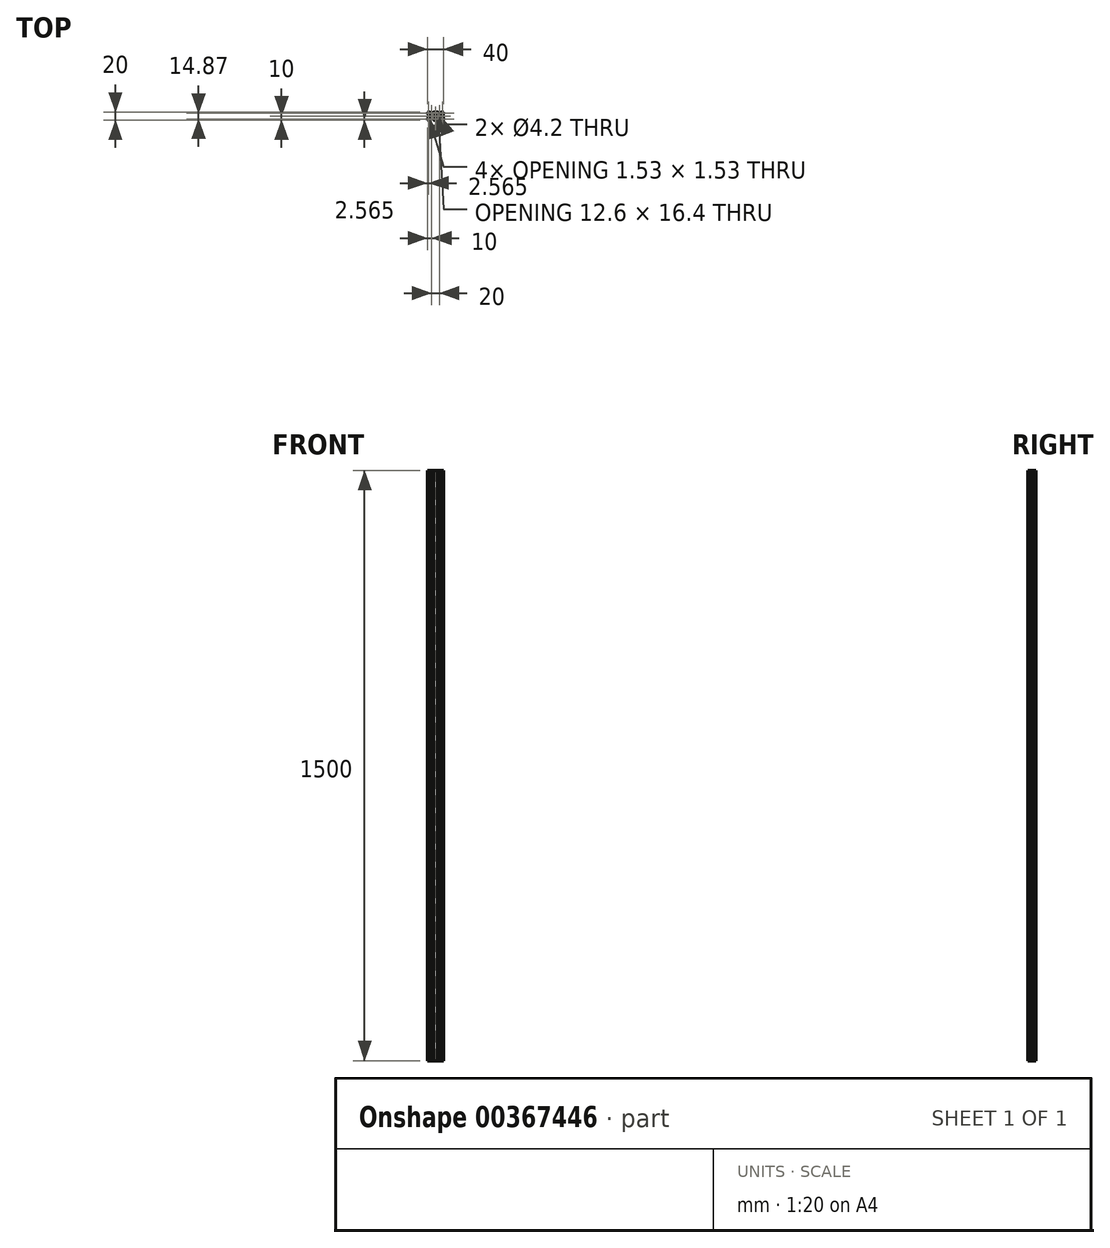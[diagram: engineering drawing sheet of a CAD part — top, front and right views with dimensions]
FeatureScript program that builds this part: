
annotation { "Feature Type Name" : "Feature", "Feature Type Description" : "" }
export const myFeature = defineFeature(function(context is Context, id is Id, definition is map)
    precondition{}
    {
        {
            var Q0;
            Q0=qCreatedBy(makeId("Top.planeOp"),FACE);
            var sketch = newSketch(context, id + "F0", { "sketchPlane" : qUnion([Q0])});
            skLineSegment(sketch, "E0.bottom", {"start": v(0, 0) * mm, "end": v(5.2, 0) * mm});
            skLineSegment(sketch, "E0.top", {"start": v(0, 20) * mm, "end": v(5.2, 20) * mm});
            skLineSegment(sketch, "E0.left", {"start": v(0, 0) * mm, "end": v(0, 5.2) * mm});
            skLineSegment(sketch, "E0.right", {"start": v(40, 0) * mm, "end": v(40, 5.2) * mm});
            skLineSegment(sketch, "E1", {"start": v(33.8, 12.84) * mm, "end": v(33.8, 7.16) * mm});
            skLineSegment(sketch, "E2", {"start": v(33.8, 12.84) * mm, "end": v(36.56, 15.6) * mm});
            skLineSegment(sketch, "E3", {"start": v(33.8, 7.16) * mm, "end": v(36.56, 4.4) * mm});
            skLineSegment(sketch, "E4", {"start": v(36.56, 15.6) * mm, "end": v(38.2, 15.6) * mm});
            skLineSegment(sketch, "E5", {"start": v(36.56, 4.4) * mm, "end": v(38.2, 4.4) * mm});
            skLineSegment(sketch, "E6", {"start": v(38.2, 13) * mm, "end": v(38.2, 15.6) * mm});
            skLineSegment(sketch, "E7", {"start": v(38.2, 7) * mm, "end": v(38.2, 4.4) * mm});
            skLineSegment(sketch, "E8.trimOffspring", {"start": v(40, 14.8) * mm, "end": v(40, 20) * mm});
            skLineSegment(sketch, "E9", {"start": v(33, 18.2) * mm, "end": v(35.6, 18.2) * mm});
            skLineSegment(sketch, "E10", {"start": v(35.6, 18.2) * mm, "end": v(35.6, 16.56) * mm});
            skLineSegment(sketch, "E11", {"start": v(35.6, 16.56) * mm, "end": v(32.84, 13.8) * mm});
            skLineSegment(sketch, "E12", {"start": v(32.84, 13.8) * mm, "end": v(27.16, 13.8) * mm});
            skLineSegment(sketch, "E13", {"start": v(27, 18.2) * mm, "end": v(24.4, 18.2) * mm});
            skLineSegment(sketch, "E14", {"start": v(24.4, 18.2) * mm, "end": v(24.4, 16.56) * mm});
            skLineSegment(sketch, "E15", {"start": v(24.4, 16.56) * mm, "end": v(27.16, 13.8) * mm});
            skLineSegment(sketch, "E16", {"start": v(33, 1.8) * mm, "end": v(35.6, 1.8) * mm});
            skLineSegment(sketch, "E17", {"start": v(35.6, 1.8) * mm, "end": v(35.6, 3.44) * mm});
            skLineSegment(sketch, "E18", {"start": v(35.6, 3.44) * mm, "end": v(32.84, 6.2) * mm});
            skLineSegment(sketch, "E19", {"start": v(32.84, 6.2) * mm, "end": v(27.16, 6.2) * mm});
            skLineSegment(sketch, "E20", {"start": v(27.16, 6.2) * mm, "end": v(24.4, 3.44) * mm});
            skLineSegment(sketch, "E21", {"start": v(24.4, 3.44) * mm, "end": v(24.4, 1.8) * mm});
            skLineSegment(sketch, "E22", {"start": v(24.4, 1.8) * mm, "end": v(27, 1.8) * mm});
            skLineSegment(sketch, "E23.trimOffspring", {"start": v(34.8, 20) * mm, "end": v(40, 20) * mm});
            skLineSegment(sketch, "E24.trimOffspring", {"start": v(34.8, 0) * mm, "end": v(40, 0) * mm});
            skLineSegment(sketch, "E25", {"start": v(7, 18.2) * mm, "end": v(4.4, 18.2) * mm});
            skLineSegment(sketch, "E26", {"start": v(4.4, 18.2) * mm, "end": v(4.4, 16.56) * mm});
            skLineSegment(sketch, "E27", {"start": v(4.4, 16.56) * mm, "end": v(7.16, 13.8) * mm});
            skLineSegment(sketch, "E28", {"start": v(7.16, 13.8) * mm, "end": v(12.84, 13.8) * mm});
            skLineSegment(sketch, "E29", {"start": v(12.84, 13.8) * mm, "end": v(15.6, 16.56) * mm});
            skLineSegment(sketch, "E30", {"start": v(15.6, 16.56) * mm, "end": v(15.6, 18.2) * mm});
            skLineSegment(sketch, "E31", {"start": v(15.6, 18.2) * mm, "end": v(13, 18.2) * mm});
            skLineSegment(sketch, "E32", {"start": v(1.8, 13) * mm, "end": v(1.8, 15.6) * mm});
            skLineSegment(sketch, "E33", {"start": v(1.8, 15.6) * mm, "end": v(3.44, 15.6) * mm});
            skLineSegment(sketch, "E34", {"start": v(3.44, 15.6) * mm, "end": v(6.2, 12.84) * mm});
            skLineSegment(sketch, "E35", {"start": v(6.2, 12.84) * mm, "end": v(6.2, 7.16) * mm});
            skLineSegment(sketch, "E36", {"start": v(6.2, 7.16) * mm, "end": v(3.44, 4.4) * mm});
            skLineSegment(sketch, "E37", {"start": v(3.44, 4.4) * mm, "end": v(1.8, 4.4) * mm});
            skLineSegment(sketch, "E38", {"start": v(1.8, 7) * mm, "end": v(1.8, 4.4) * mm});
            skLineSegment(sketch, "E39", {"start": v(7, 1.8) * mm, "end": v(4.4, 1.8) * mm});
            skLineSegment(sketch, "E40", {"start": v(4.4, 1.8) * mm, "end": v(4.4, 3.44) * mm});
            skLineSegment(sketch, "E41", {"start": v(4.4, 3.44) * mm, "end": v(7.16, 6.2) * mm});
            skLineSegment(sketch, "E42", {"start": v(7.16, 6.2) * mm, "end": v(12.84, 6.2) * mm});
            skLineSegment(sketch, "E43", {"start": v(12.84, 6.2) * mm, "end": v(15.6, 3.44) * mm});
            skLineSegment(sketch, "E44", {"start": v(15.6, 3.44) * mm, "end": v(15.6, 1.8) * mm});
            skLineSegment(sketch, "E45", {"start": v(15.6, 1.8) * mm, "end": v(13, 1.8) * mm});
            skLineSegment(sketch, "E46.trimOffspring", {"start": v(14.8, 20) * mm, "end": v(25.2, 20) * mm});
            skLineSegment(sketch, "E47.trimOffspring", {"start": v(0, 14.8) * mm, "end": v(0, 20) * mm});
            skLineSegment(sketch, "E48.trimOffspring", {"start": v(14.8, 0) * mm, "end": v(25.2, 0) * mm});
            skLineSegment(sketch, "E49", {"start": v(38.2, 7) * mm, "end": v(40, 5.2) * mm});
            skLineSegment(sketch, "E50", {"start": v(38.2, 13) * mm, "end": v(40, 14.8) * mm});
            skLineSegment(sketch, "E51", {"start": v(33, 1.8) * mm, "end": v(34.8, 0) * mm});
            skLineSegment(sketch, "E52", {"start": v(27, 1.8) * mm, "end": v(25.2, 0) * mm});
            skLineSegment(sketch, "E53", {"start": v(13, 1.8) * mm, "end": v(14.8, 0) * mm});
            skLineSegment(sketch, "E54", {"start": v(7, 1.8) * mm, "end": v(5.2, 0) * mm});
            skLineSegment(sketch, "E55", {"start": v(1.8, 7) * mm, "end": v(0, 5.2) * mm});
            skLineSegment(sketch, "E56", {"start": v(1.8, 13) * mm, "end": v(0, 14.8) * mm});
            skLineSegment(sketch, "E57", {"start": v(7, 18.2) * mm, "end": v(5.2, 20) * mm});
            skLineSegment(sketch, "E58", {"start": v(13, 18.2) * mm, "end": v(14.8, 20) * mm});
            skLineSegment(sketch, "E59", {"start": v(27, 18.2) * mm, "end": v(25.2, 20) * mm});
            skLineSegment(sketch, "E60", {"start": v(33, 18.2) * mm, "end": v(34.8, 20) * mm});
            skPoint(sketch, "E61.start.orphan", {"position": v(7, 0) * mm});
            skSolve(sketch);
        }
        {
            var Q0;
            Q0=qSketchRegion(id+"F0",true);
            extrude(context, id + "F1", {"entities" : qUnion([Q0]), "depth" : 1500 * mm});
        }
        {
            var Q0;
            Q0=makeQuery(id+"F1.opExtrude","CAP_FACE",FACE,{"disambiguationData":[OSD([sQuery(id+"F0.wireOp",EDGE,"E0.bottom"),sQuery(id+"F0.wireOp",EDGE,"E0.top"),sQuery(id+"F0.wireOp",EDGE,"E0.left"),sQuery(id+"F0.wireOp",EDGE,"E0.right"),sQuery(id+"F0.wireOp",EDGE,"E1"),sQuery(id+"F0.wireOp",EDGE,"E2"),sQuery(id+"F0.wireOp",EDGE,"E3"),sQuery(id+"F0.wireOp",EDGE,"E4"),sQuery(id+"F0.wireOp",EDGE,"E5"),sQuery(id+"F0.wireOp",EDGE,"E6"),sQuery(id+"F0.wireOp",EDGE,"E7"),sQuery(id+"F0.wireOp",EDGE,"E8.trimOffspring"),sQuery(id+"F0.wireOp",EDGE,"E9"),sQuery(id+"F0.wireOp",EDGE,"E10"),sQuery(id+"F0.wireOp",EDGE,"E11"),sQuery(id+"F0.wireOp",EDGE,"E12"),sQuery(id+"F0.wireOp",EDGE,"E13"),sQuery(id+"F0.wireOp",EDGE,"E14"),sQuery(id+"F0.wireOp",EDGE,"E15"),sQuery(id+"F0.wireOp",EDGE,"E16"),sQuery(id+"F0.wireOp",EDGE,"E17"),sQuery(id+"F0.wireOp",EDGE,"E18"),sQuery(id+"F0.wireOp",EDGE,"E19"),sQuery(id+"F0.wireOp",EDGE,"E20"),sQuery(id+"F0.wireOp",EDGE,"E21"),sQuery(id+"F0.wireOp",EDGE,"E22"),sQuery(id+"F0.wireOp",EDGE,"E23.trimOffspring"),sQuery(id+"F0.wireOp",EDGE,"E24.trimOffspring"),sQuery(id+"F0.wireOp",EDGE,"E25"),sQuery(id+"F0.wireOp",EDGE,"E26"),sQuery(id+"F0.wireOp",EDGE,"E27"),sQuery(id+"F0.wireOp",EDGE,"E28"),sQuery(id+"F0.wireOp",EDGE,"E29"),sQuery(id+"F0.wireOp",EDGE,"E30"),sQuery(id+"F0.wireOp",EDGE,"E31"),sQuery(id+"F0.wireOp",EDGE,"E32"),sQuery(id+"F0.wireOp",EDGE,"E33"),sQuery(id+"F0.wireOp",EDGE,"E34"),sQuery(id+"F0.wireOp",EDGE,"E35"),sQuery(id+"F0.wireOp",EDGE,"E36"),sQuery(id+"F0.wireOp",EDGE,"E37"),sQuery(id+"F0.wireOp",EDGE,"E38"),sQuery(id+"F0.wireOp",EDGE,"E39"),sQuery(id+"F0.wireOp",EDGE,"E40"),sQuery(id+"F0.wireOp",EDGE,"E41"),sQuery(id+"F0.wireOp",EDGE,"E42"),sQuery(id+"F0.wireOp",EDGE,"E43"),sQuery(id+"F0.wireOp",EDGE,"E44"),sQuery(id+"F0.wireOp",EDGE,"E45"),sQuery(id+"F0.wireOp",EDGE,"E46.trimOffspring"),sQuery(id+"F0.wireOp",EDGE,"E47.trimOffspring"),sQuery(id+"F0.wireOp",EDGE,"E48.trimOffspring"),sQuery(id+"F0.wireOp",EDGE,"E49"),sQuery(id+"F0.wireOp",EDGE,"E50"),sQuery(id+"F0.wireOp",EDGE,"E51"),sQuery(id+"F0.wireOp",EDGE,"E52"),sQuery(id+"F0.wireOp",EDGE,"E53"),sQuery(id+"F0.wireOp",EDGE,"E54"),sQuery(id+"F0.wireOp",EDGE,"E55"),sQuery(id+"F0.wireOp",EDGE,"E56"),sQuery(id+"F0.wireOp",EDGE,"E57"),sQuery(id+"F0.wireOp",EDGE,"E58"),sQuery(id+"F0.wireOp",EDGE,"E59"),sQuery(id+"F0.wireOp",EDGE,"E60")])],"isStart":false});
            var sketch = newSketch(context, id + "F2", { "sketchPlane" : qUnion([Q0])});
            skLineSegment(sketch, "E62", {"start": v(1.8, 18.2) * mm, "end": v(1.8, 16.67) * mm});
            skLineSegment(sketch, "E63", {"start": v(1.8, 16.67) * mm, "end": v(3.33, 18.2) * mm});
            skLineSegment(sketch, "E64", {"start": v(3.33, 18.2) * mm, "end": v(1.8, 18.2) * mm});
            skLineSegment(sketch, "E65", {"start": v(1.8, 1.8) * mm, "end": v(3.33, 1.8) * mm});
            skLineSegment(sketch, "E66", {"start": v(3.33, 1.8) * mm, "end": v(1.8, 3.33) * mm});
            skLineSegment(sketch, "E67", {"start": v(1.8, 3.33) * mm, "end": v(1.8, 1.8) * mm});
            skLineSegment(sketch, "E68", {"start": v(38.2, 1.8) * mm, "end": v(38.2, 3.33) * mm});
            skLineSegment(sketch, "E69", {"start": v(38.2, 3.33) * mm, "end": v(36.67, 1.8) * mm});
            skLineSegment(sketch, "E70", {"start": v(36.67, 1.8) * mm, "end": v(38.2, 1.8) * mm});
            skLineSegment(sketch, "E71", {"start": v(38.2, 18.2) * mm, "end": v(38.2, 16.67) * mm});
            skLineSegment(sketch, "E72", {"start": v(38.2, 16.67) * mm, "end": v(36.67, 18.2) * mm});
            skLineSegment(sketch, "E73", {"start": v(36.67, 18.2) * mm, "end": v(38.2, 18.2) * mm});
            skSolve(sketch);
        }
        {
            var Q0;
            Q0=qSketchRegion(id+"F2",true);
            extrude(context, id + "F3", {"entities" : qUnion([Q0]), "operationType" : NewBodyOperationType.REMOVE, "endBound" : BoundingType.THROUGH_ALL, "oppositeDirection" : true, "depth" : 25 * mm});
        }
        {
            var Q0;
            Q0=makeQuery(id+"F1.opExtrude","CAP_FACE",FACE,{"disambiguationData":[OSD([sQuery(id+"F0.wireOp",EDGE,"E0.bottom"),sQuery(id+"F0.wireOp",EDGE,"E0.top"),sQuery(id+"F0.wireOp",EDGE,"E0.left"),sQuery(id+"F0.wireOp",EDGE,"E0.right"),sQuery(id+"F0.wireOp",EDGE,"E1"),sQuery(id+"F0.wireOp",EDGE,"E2"),sQuery(id+"F0.wireOp",EDGE,"E3"),sQuery(id+"F0.wireOp",EDGE,"E4"),sQuery(id+"F0.wireOp",EDGE,"E5"),sQuery(id+"F0.wireOp",EDGE,"E6"),sQuery(id+"F0.wireOp",EDGE,"E7"),sQuery(id+"F0.wireOp",EDGE,"E8.trimOffspring"),sQuery(id+"F0.wireOp",EDGE,"E9"),sQuery(id+"F0.wireOp",EDGE,"E10"),sQuery(id+"F0.wireOp",EDGE,"E11"),sQuery(id+"F0.wireOp",EDGE,"E12"),sQuery(id+"F0.wireOp",EDGE,"E13"),sQuery(id+"F0.wireOp",EDGE,"E14"),sQuery(id+"F0.wireOp",EDGE,"E15"),sQuery(id+"F0.wireOp",EDGE,"E16"),sQuery(id+"F0.wireOp",EDGE,"E17"),sQuery(id+"F0.wireOp",EDGE,"E18"),sQuery(id+"F0.wireOp",EDGE,"E19"),sQuery(id+"F0.wireOp",EDGE,"E20"),sQuery(id+"F0.wireOp",EDGE,"E21"),sQuery(id+"F0.wireOp",EDGE,"E22"),sQuery(id+"F0.wireOp",EDGE,"E23.trimOffspring"),sQuery(id+"F0.wireOp",EDGE,"E24.trimOffspring"),sQuery(id+"F0.wireOp",EDGE,"E25"),sQuery(id+"F0.wireOp",EDGE,"E26"),sQuery(id+"F0.wireOp",EDGE,"E27"),sQuery(id+"F0.wireOp",EDGE,"E28"),sQuery(id+"F0.wireOp",EDGE,"E29"),sQuery(id+"F0.wireOp",EDGE,"E30"),sQuery(id+"F0.wireOp",EDGE,"E31"),sQuery(id+"F0.wireOp",EDGE,"E32"),sQuery(id+"F0.wireOp",EDGE,"E33"),sQuery(id+"F0.wireOp",EDGE,"E34"),sQuery(id+"F0.wireOp",EDGE,"E35"),sQuery(id+"F0.wireOp",EDGE,"E36"),sQuery(id+"F0.wireOp",EDGE,"E37"),sQuery(id+"F0.wireOp",EDGE,"E38"),sQuery(id+"F0.wireOp",EDGE,"E39"),sQuery(id+"F0.wireOp",EDGE,"E40"),sQuery(id+"F0.wireOp",EDGE,"E41"),sQuery(id+"F0.wireOp",EDGE,"E42"),sQuery(id+"F0.wireOp",EDGE,"E43"),sQuery(id+"F0.wireOp",EDGE,"E44"),sQuery(id+"F0.wireOp",EDGE,"E45"),sQuery(id+"F0.wireOp",EDGE,"E46.trimOffspring"),sQuery(id+"F0.wireOp",EDGE,"E47.trimOffspring"),sQuery(id+"F0.wireOp",EDGE,"E48.trimOffspring"),sQuery(id+"F0.wireOp",EDGE,"E49"),sQuery(id+"F0.wireOp",EDGE,"E50"),sQuery(id+"F0.wireOp",EDGE,"E51"),sQuery(id+"F0.wireOp",EDGE,"E52"),sQuery(id+"F0.wireOp",EDGE,"E53"),sQuery(id+"F0.wireOp",EDGE,"E54"),sQuery(id+"F0.wireOp",EDGE,"E55"),sQuery(id+"F0.wireOp",EDGE,"E56"),sQuery(id+"F0.wireOp",EDGE,"E57"),sQuery(id+"F0.wireOp",EDGE,"E58"),sQuery(id+"F0.wireOp",EDGE,"E59"),sQuery(id+"F0.wireOp",EDGE,"E60")])],"isStart":false});
            var sketch = newSketch(context, id + "F4", { "sketchPlane" : qUnion([Q0])});
            skLineSegment(sketch, "E74", {"start": v(17.1, 18.2) * mm, "end": v(22.9, 18.2) * mm});
            skLineSegment(sketch, "E75", {"start": v(22.9, 1.8) * mm, "end": v(17.1, 1.8) * mm});
            skLineSegment(sketch, "E76", {"start": v(17.1, 1.8) * mm, "end": v(17.1, 3.76) * mm});
            skLineSegment(sketch, "E77", {"start": v(22.9, 1.8) * mm, "end": v(22.9, 3.76) * mm});
            skLineSegment(sketch, "E78", {"start": v(22.9, 18.2) * mm, "end": v(22.9, 16.24) * mm});
            skLineSegment(sketch, "E79", {"start": v(17.1, 18.2) * mm, "end": v(17.1, 16.24) * mm});
            skLineSegment(sketch, "E80", {"start": v(22.9, 16.24) * mm, "end": v(26.3, 12.84) * mm});
            skLineSegment(sketch, "E81", {"start": v(26.3, 12.84) * mm, "end": v(26.3, 7.16) * mm});
            skLineSegment(sketch, "E82", {"start": v(26.3, 7.16) * mm, "end": v(22.9, 3.76) * mm});
            skLineSegment(sketch, "E83", {"start": v(17.1, 3.76) * mm, "end": v(13.7, 7.16) * mm});
            skLineSegment(sketch, "E84", {"start": v(13.7, 7.16) * mm, "end": v(13.7, 12.84) * mm});
            skLineSegment(sketch, "E85", {"start": v(13.7, 12.84) * mm, "end": v(17.1, 16.24) * mm});
            skCircle(sketch, "E86", {"center": v(30, 10) * mm, "radius": 2.1 * mm});
            skPoint(sketch, "E86.centerSnap0", {"position": v(30, 13.8) * mm});
            skPoint(sketch, "E86.centerSnap1", {"position": v(26.3, 10) * mm});
            skCircle(sketch, "E87", {"center": v(10, 10) * mm, "radius": 2.1 * mm});
            skPoint(sketch, "E87.centerSnap0", {"position": v(10, 13.8) * mm});
            skPoint(sketch, "E87.centerSnap1", {"position": v(13.7, 10) * mm});
            skSolve(sketch);
        }
        {
            var Q0;
            Q0=qSketchRegion(id+"F4",true);
            extrude(context, id + "F5", {"entities" : qUnion([Q0]), "operationType" : NewBodyOperationType.REMOVE, "endBound" : BoundingType.THROUGH_ALL, "oppositeDirection" : true, "depth" : 25 * mm});
        }
    });
